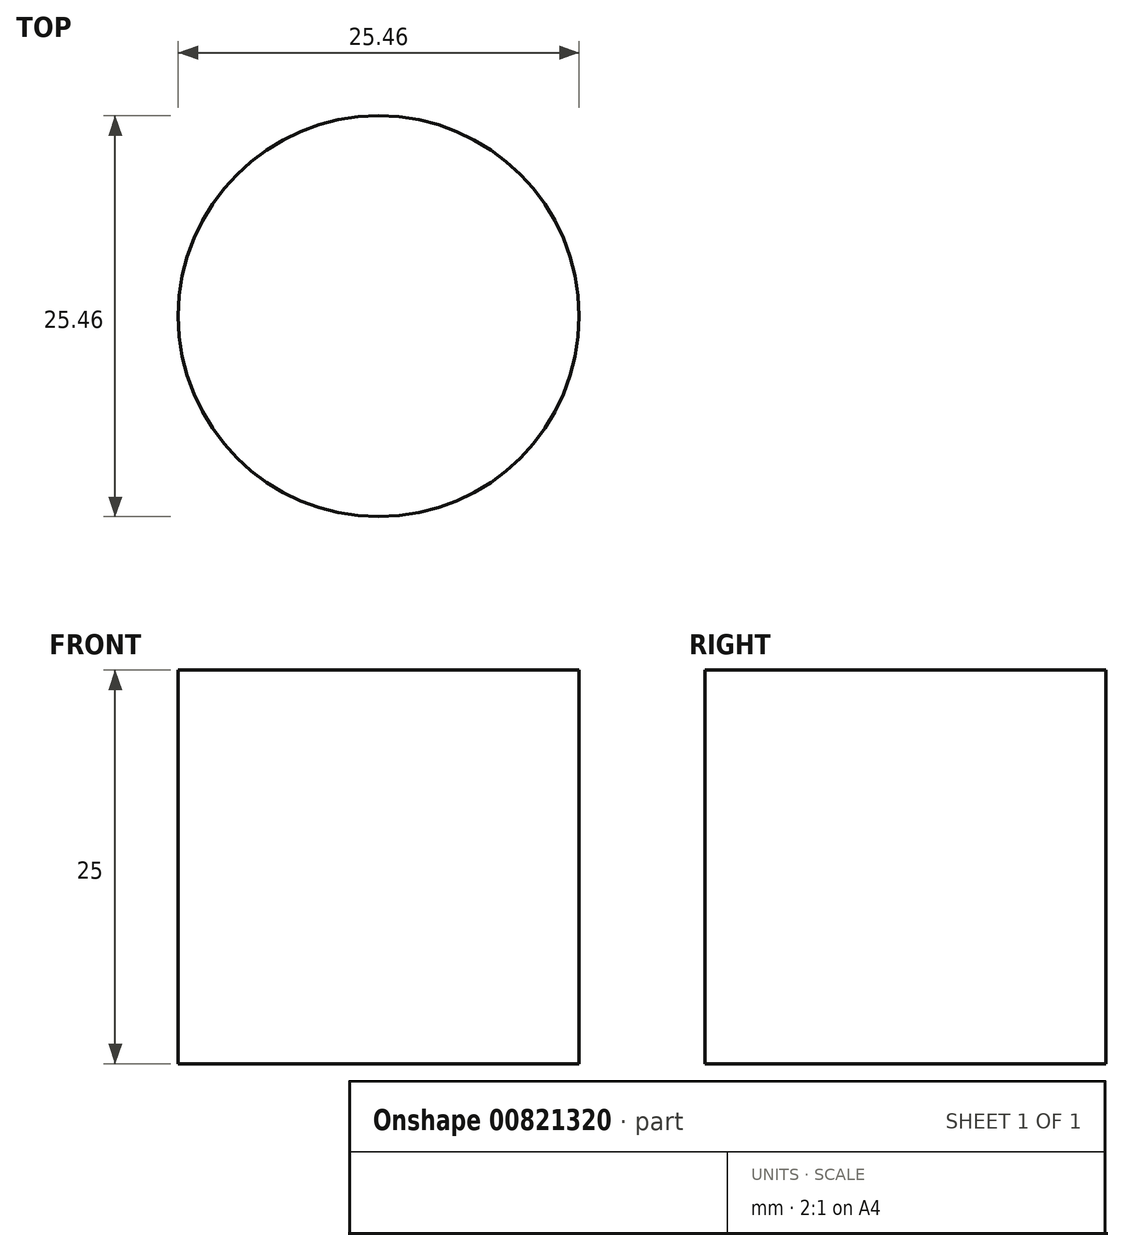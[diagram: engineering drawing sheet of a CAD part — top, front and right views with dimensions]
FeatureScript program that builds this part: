
annotation { "Feature Type Name" : "Feature", "Feature Type Description" : "" }
export const myFeature = defineFeature(function(context is Context, id is Id, definition is map)
    precondition{}
    {
        {
            var Q0;
            Q0=qCreatedBy(makeId("Top.planeOp"),FACE);
            var sketch = newSketch(context, id + "F0", { "sketchPlane" : qUnion([Q0])});
            skCircle(sketch, "E0", {"center": v(1.4, 0) * mm, "radius": 12.73 * mm});
            skSolve(sketch);
        }
        {
            var Q0;
            Q0=makeQuery(id+"F0.imprint","IMPRINT",FACE,{"disambiguationData":[TD([[makeQuery(id+"F0.imprint","IMPRINT",EDGE,{"derivedFrom":sQuery(id+"F0.wireOp",EDGE,"E0")}),1.0]])]});
            extrude(context, id + "F1", {"entities" : qUnion([Q0]), "depth" : 25 * mm, "offsetDistance" : 25 * mm});
        }
    });
